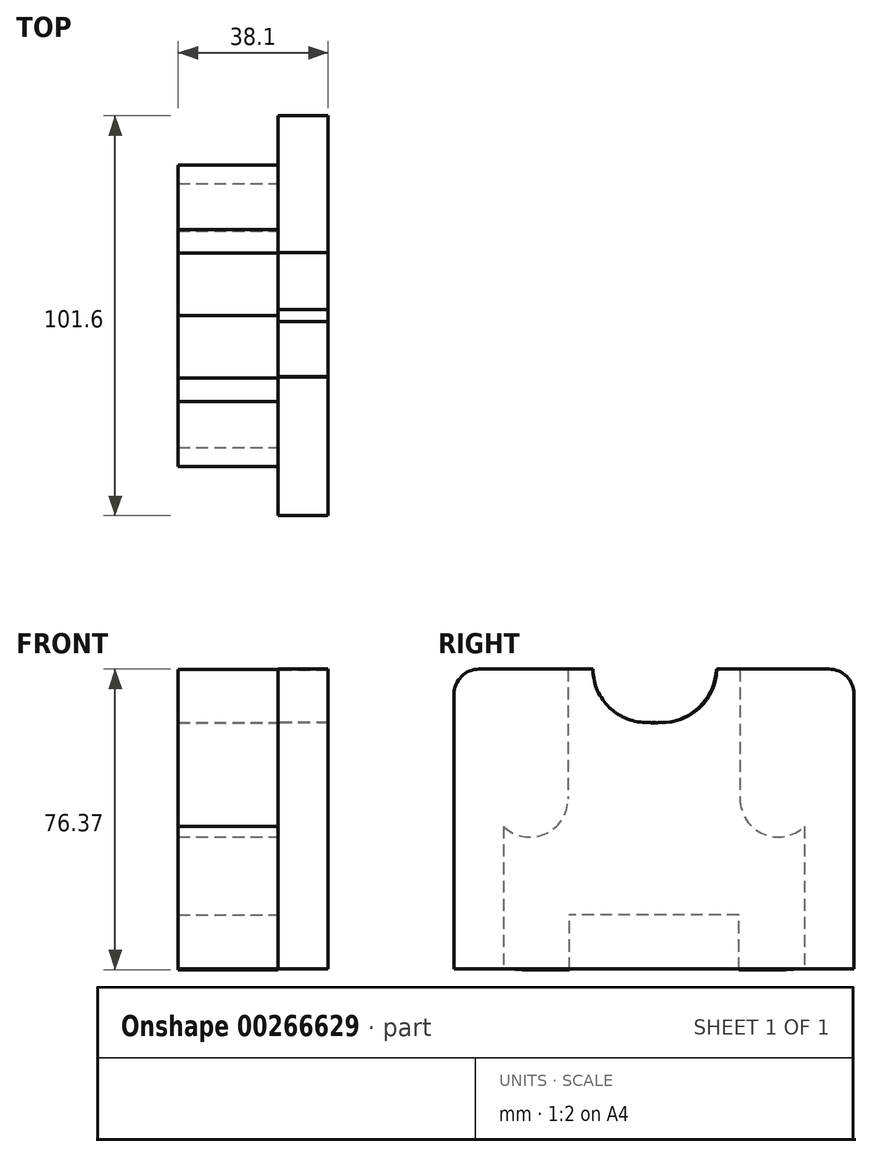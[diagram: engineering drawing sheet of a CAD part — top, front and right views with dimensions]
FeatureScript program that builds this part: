
annotation { "Feature Type Name" : "Feature", "Feature Type Description" : "" }
export const myFeature = defineFeature(function(context is Context, id is Id, definition is map)
    precondition{}
    {
        {
            var Q0;
            Q0=qCreatedBy(makeId("Right.planeOp"),FACE);
            var sketch = newSketch(context, id + "F0", { "sketchPlane" : qUnion([Q0])});
            skLineSegment(sketch, "E0.bottom", {"start": v(44.45, 38.1) * mm, "end": v(-44.45, 38.1) * mm});
            skLineSegment(sketch, "E0.top", {"start": v(50.8, -38.1) * mm, "end": v(-50.8, -38.1) * mm});
            skLineSegment(sketch, "E0.left", {"start": v(50.8, 31.75) * mm, "end": v(50.8, -38.1) * mm});
            skLineSegment(sketch, "E0.right", {"start": v(-50.8, 31.75) * mm, "end": v(-50.8, -38.1) * mm});
            skPoint(sketch, "E0.middle", {"position": v(0, 0) * mm});
            skPoint(sketch, "E1.visualSharp", {"position": v(-50.8, 38.1) * mm});
            skArc(sketch, "E1.filletArc", {"start": v(-44.45, 38.1) * mm, "mid": v(-48.94, 36.24) * mm, "end": v(-50.8, 31.75) * mm});
            skPoint(sketch, "E2.visualSharp", {"position": v(50.8, 38.1) * mm});
            skArc(sketch, "E2.filletArc", {"start": v(50.8, 31.75) * mm, "mid": v(48.94, 36.24) * mm, "end": v(44.45, 38.1) * mm});
            skSolve(sketch);
        }
        {
            var Q0;
            Q0=makeQuery(id+"F0.imprint","IMPRINT",FACE,{"disambiguationData":[TD([[makeQuery(id+"F0.imprint","IMPRINT",EDGE,{"derivedFrom":sQuery(id+"F0.wireOp",EDGE,"E0.bottom")}),1.0]])]});
            extrude(context, id + "F1", {"entities" : qUnion([Q0]), "depth" : 12.7 * mm});
        }
        {
            var Q0;
            Q0=qCreatedBy(makeId("Right.planeOp"),FACE);
            var sketch = newSketch(context, id + "F2", { "sketchPlane" : qUnion([Q0])});
            skArc(sketch, "E3", {"start": v(-15.87, 38.02) * mm, "mid": v(-10.83, 27.87) * mm, "end": v(0, 24.55) * mm});
            skLineSegment(sketch, "E4", {"start": v(-15.87, 38.02) * mm, "end": v(-21.85, 38.02) * mm});
            skLineSegment(sketch, "E5", {"start": v(-33.53, -38.27) * mm, "end": v(-21.54, -38.27) * mm});
            skLineSegment(sketch, "E6", {"start": v(-21.54, -38.27) * mm, "end": v(-21.54, -24.3) * mm});
            skLineSegment(sketch, "E7", {"start": v(-21.54, -24.3) * mm, "end": v(0, -24.3) * mm});
            skLineSegment(sketch, "E8", {"start": v(-21.85, 38.02) * mm, "end": v(-21.85, 5.13) * mm});
            skArc(sketch, "E9", {"start": v(-38.26, -1.86) * mm, "mid": v(-27.75, -3.79) * mm, "end": v(-21.85, 5.13) * mm});
            skLineSegment(sketch, "E10", {"start": v(-38.26, -1.86) * mm, "end": v(-38.26, -38.06) * mm});
            skLineSegment(sketch, "E11", {"start": v(-38.26, -38.06) * mm, "end": v(-33.53, -38.27) * mm});
            skLineSegment(sketch, "E12", {"start": v(0, 24.55) * mm, "end": v(0, -24.3) * mm});
            skArc(sketch, "E13.MirrorCS", {"start": v(15.87, 38.02) * mm, "mid": v(10.83, 27.87) * mm, "end": v(0, 24.55) * mm});
            skLineSegment(sketch, "E14.MirrorCS", {"start": v(15.87, 38.02) * mm, "end": v(21.85, 38.02) * mm});
            skLineSegment(sketch, "E15.MirrorCS", {"start": v(21.85, 38.02) * mm, "end": v(21.85, 5.13) * mm});
            skArc(sketch, "E16.MirrorCS", {"start": v(38.26, -1.86) * mm, "mid": v(27.75, -3.79) * mm, "end": v(21.85, 5.13) * mm});
            skLineSegment(sketch, "E17.MirrorCS", {"start": v(38.26, -1.86) * mm, "end": v(38.26, -38.06) * mm});
            skLineSegment(sketch, "E18.MirrorCS", {"start": v(38.26, -38.06) * mm, "end": v(33.53, -38.27) * mm});
            skLineSegment(sketch, "E19.MirrorCS", {"start": v(33.53, -38.27) * mm, "end": v(21.54, -38.27) * mm});
            skLineSegment(sketch, "E20.MirrorCS", {"start": v(21.54, -38.27) * mm, "end": v(21.54, -24.3) * mm});
            skLineSegment(sketch, "E21.MirrorCS", {"start": v(21.54, -24.3) * mm, "end": v(0, -24.3) * mm});
            skSolve(sketch);
        }
        {
            var Q0;
            Q0=makeQuery(id+"F2.imprint","IMPRINT",FACE,{"disambiguationData":[TD([[makeQuery(id+"F2.imprint","IMPRINT",EDGE,{"derivedFrom":sQuery(id+"F2.wireOp",EDGE,"E12")}),1.0]])]});
            var Q1;
            Q1=makeQuery(id+"F2.imprint","IMPRINT",FACE,{"disambiguationData":[TD([[makeQuery(id+"F2.imprint","IMPRINT",EDGE,{"derivedFrom":sQuery(id+"F2.wireOp",EDGE,"E3")}),-1.0]])]});
            extrude(context, id + "F3", {"entities" : qUnion([Q0, Q1]), "operationType" : NewBodyOperationType.ADD, "oppositeDirection" : true, "depth" : 25.4 * mm});
        }
        {
            var Q0;
            Q0=qCreatedBy(makeId("Right.planeOp"),FACE);
            var sketch = newSketch(context, id + "F4", { "sketchPlane" : qUnion([Q0])});
            skArc(sketch, "E22", {"start": v(-15.7, 40.04) * mm, "mid": v(0.2, 24.47) * mm, "end": v(15.92, 40.22) * mm});
            skLineSegment(sketch, "E23", {"start": v(15.92, 40.22) * mm, "end": v(-15.7, 40.04) * mm});
            skSolve(sketch);
        }
        {
            var Q0;
            Q0=makeQuery(id+"F4.imprint","IMPRINT",FACE,{"disambiguationData":[TD([[makeQuery(id+"F4.imprint","IMPRINT",EDGE,{"derivedFrom":sQuery(id+"F4.wireOp",EDGE,"E22")}),1.0]])]});
            extrude(context, id + "F5", {"entities" : qUnion([Q0]), "operationType" : NewBodyOperationType.REMOVE, "depth" : 76.2 * mm});
        }
        {
            var Q0;
            Q0=qCreatedBy(makeId("Right.planeOp"),FACE);
            var sketch = newSketch(context, id + "F6", { "sketchPlane" : qUnion([Q0])});
            skArc(sketch, "E24", {"start": v(-15.37, 40.1) * mm, "mid": v(-11.55, 28.54) * mm, "end": v(0, 24.69) * mm});
            skArc(sketch, "E25", {"start": v(0, 24.69) * mm, "mid": v(11.83, 28.55) * mm, "end": v(15.9, 40.3) * mm});
            skLineSegment(sketch, "E26", {"start": v(15.9, 40.3) * mm, "end": v(-15.37, 40.1) * mm});
            skSolve(sketch);
        }
        {
            var Q0;
            Q0=makeQuery(id+"F6.imprint","IMPRINT",FACE,{"disambiguationData":[TD([[makeQuery(id+"F6.imprint","IMPRINT",EDGE,{"derivedFrom":sQuery(id+"F6.wireOp",EDGE,"E24")}),1.0]])]});
            extrude(context, id + "F7", {"entities" : qUnion([Q0]), "operationType" : NewBodyOperationType.REMOVE, "depth" : 25.4 * mm});
        }
    });
